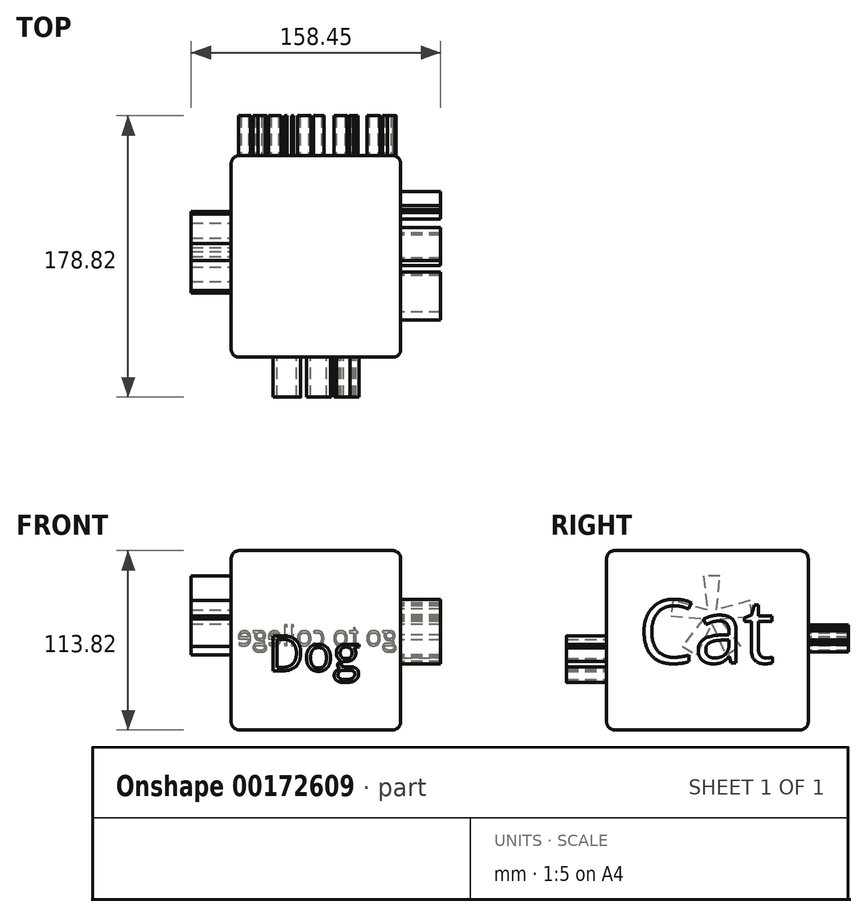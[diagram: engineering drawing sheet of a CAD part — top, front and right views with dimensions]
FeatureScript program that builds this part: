
annotation { "Feature Type Name" : "Feature", "Feature Type Description" : "" }
export const myFeature = defineFeature(function(context is Context, id is Id, definition is map)
    precondition{}
    {
        {
            var Q0;
            Q0=qCreatedBy(makeId("Front.planeOp"),FACE);
            var sketch = newSketch(context, id + "F0", { "sketchPlane" : qUnion([Q0])});
            skLineSegment(sketch, "E0.bottom", {"start": v(-56.12, 53.95) * mm, "end": v(51.53, 53.95) * mm});
            skLineSegment(sketch, "E0.top", {"start": v(-56.12, -59.87) * mm, "end": v(51.53, -59.87) * mm});
            skLineSegment(sketch, "E0.left", {"start": v(-56.12, 53.95) * mm, "end": v(-56.12, -59.87) * mm});
            skLineSegment(sketch, "E0.right", {"start": v(51.53, 53.95) * mm, "end": v(51.53, -59.87) * mm});
            skSolve(sketch);
        }
        {
            var Q0;
            Q0 = qSketchRegion(id + "F0", true);
            extrude(context, id + "F1", {"entities" : qUnion([Q0]), "depth" : 128.02 * mm});
        }
        {
            var Q0;
            Q0=makeQuery(id+"F1.opExtrude","SWEPT_EDGE",EDGE,{"disambiguationData":[OSD([sQuery(id+"F0.wireOp",EDGE,"E0.top"),sQuery(id+"F0.wireOp",EDGE,"E0.left")])]});
            var Q1;
            Q1=makeQuery(id+"F1.opExtrude","CAP_FACE",FACE,{"disambiguationData":[OSD([sQuery(id+"F0.wireOp",EDGE,"E0.bottom"),sQuery(id+"F0.wireOp",EDGE,"E0.top"),sQuery(id+"F0.wireOp",EDGE,"E0.left"),sQuery(id+"F0.wireOp",EDGE,"E0.right")])],"isStart":true});
            var Q2;
            Q2=makeQuery(id+"F1.opExtrude","SWEPT_EDGE",EDGE,{"disambiguationData":[OSD([sQuery(id+"F0.wireOp",EDGE,"E0.bottom"),sQuery(id+"F0.wireOp",EDGE,"E0.right")])]});
            var Q3;
            Q3=makeQuery(id+"F1.opExtrude","SWEPT_FACE",FACE,{"disambiguationData":[OSD([sQuery(id+"F0.wireOp",EDGE,"E0.bottom")])]});
            var Q4;
            Q4=makeQuery(id+"F1.opExtrude","SWEPT_EDGE",EDGE,{"disambiguationData":[OSD([sQuery(id+"F0.wireOp",EDGE,"E0.bottom"),sQuery(id+"F0.wireOp",EDGE,"E0.left")])]});
            var Q5;
            Q5=makeQuery(id+"F1.opExtrude","CAP_EDGE",EDGE,{"disambiguationData":[OSD([sQuery(id+"F0.wireOp",EDGE,"E0.bottom")])],"isStart":true});
            var Q6;
            Q6=makeQuery(id+"F1.opExtrude","SWEPT_FACE",FACE,{"disambiguationData":[OSD([sQuery(id+"F0.wireOp",EDGE,"E0.left")])]});
            var Q7;
            Q7=makeQuery(id+"F1.opExtrude","CAP_EDGE",EDGE,{"disambiguationData":[OSD([sQuery(id+"F0.wireOp",EDGE,"E0.bottom")])],"isStart":false});
            var Q8;
            Q8=makeQuery(id+"F1.opExtrude","CAP_EDGE",EDGE,{"disambiguationData":[OSD([sQuery(id+"F0.wireOp",EDGE,"E0.top")])],"isStart":true});
            var Q9;
            Q9=makeQuery(id+"F1.opExtrude","CAP_EDGE",EDGE,{"disambiguationData":[OSD([sQuery(id+"F0.wireOp",EDGE,"E0.right")])],"isStart":true});
            var Q10;
            Q10=makeQuery(id+"F1.opExtrude","CAP_EDGE",EDGE,{"disambiguationData":[OSD([sQuery(id+"F0.wireOp",EDGE,"E0.left")])],"isStart":true});
            var Q11;
            Q11=makeQuery(id+"F1.opExtrude","CAP_EDGE",EDGE,{"disambiguationData":[OSD([sQuery(id+"F0.wireOp",EDGE,"E0.left")])],"isStart":false});
            fillet(context, id + "F2", {"entities" : qUnion([Q0, Q1, Q2, Q3, Q4, Q5, Q6, Q7, Q8, Q9, Q10, Q11]), "radius" : 5.08 * mm, "tangentPropagation" : true, "allowEdgeOverflow" : false});
        }
        {
            var Q0;
            Q0=makeQuery(id+"F2.opFillet","BLEND_FACE",FACE,{"disambiguationData":[OSD([sQuery(id+"F0.wireOp",EDGE,"E0.right")])]});
            var Q1;
            Q1=makeQuery(id+"F1.opExtrude","SWEPT_FACE",FACE,{"disambiguationData":[OSD([sQuery(id+"F0.wireOp",EDGE,"E0.top")])]});
            var Q2;
            Q2=makeQuery(id+"F1.opExtrude","SWEPT_FACE",FACE,{"disambiguationData":[OSD([sQuery(id+"F0.wireOp",EDGE,"E0.right")])]});
            var Q3;
            Q3=makeQuery(id+"F1.opExtrude","SWEPT_EDGE",EDGE,{"disambiguationData":[OSD([sQuery(id+"F0.wireOp",EDGE,"E0.top"),sQuery(id+"F0.wireOp",EDGE,"E0.right")])]});
            var Q4;
            Q4=makeQuery(id+"F1.opExtrude","CAP_FACE",FACE,{"disambiguationData":[OSD([sQuery(id+"F0.wireOp",EDGE,"E0.bottom"),sQuery(id+"F0.wireOp",EDGE,"E0.top"),sQuery(id+"F0.wireOp",EDGE,"E0.left"),sQuery(id+"F0.wireOp",EDGE,"E0.right")])],"isStart":true});
            var Q5;
            {var subQ0=sQuery(id+"F0.wireOp",EDGE,"E0.right");Q5=makeQuery(id+"F2.opFillet","BLEND_EDGE",EDGE,{"blendedFrom":[makeQuery(id+"F1.opExtrude","CAP_EDGE",EDGE,{"disambiguationData":[OSD([subQ0])],"isStart":true}),makeQuery(id+"F1.opExtrude","CAP_FACE",FACE,{"disambiguationData":[OSD([sQuery(id+"F0.wireOp",EDGE,"E0.bottom"),sQuery(id+"F0.wireOp",EDGE,"E0.top"),sQuery(id+"F0.wireOp",EDGE,"E0.left"),subQ0])],"isStart":true})],"blendedInto":[makeQuery(id+"F1.opExtrude","CAP_FACE",FACE,{"disambiguationData":[OSD([sQuery(id+"F0.wireOp",EDGE,"E0.bottom"),sQuery(id+"F0.wireOp",EDGE,"E0.top"),sQuery(id+"F0.wireOp",EDGE,"E0.left"),subQ0])],"isStart":true})]});}
            var Q6;
            {var subQ0=sQuery(id+"F0.wireOp",EDGE,"E0.right");Q6=makeQuery(id+"F2.opFillet","BLEND_EDGE",EDGE,{"blendedFrom":[makeQuery(id+"F1.opExtrude","CAP_EDGE",EDGE,{"disambiguationData":[OSD([subQ0])],"isStart":true}),makeQuery(id+"F1.opExtrude","SWEPT_FACE",FACE,{"disambiguationData":[OSD([subQ0])]})],"blendedInto":[makeQuery(id+"F1.opExtrude","SWEPT_FACE",FACE,{"disambiguationData":[OSD([subQ0])]})]});}
            fillet(context, id + "F3", {"entities" : qUnion([Q0, Q1, Q2, Q3, Q4, Q5, Q6]), "radius" : 5.08 * mm, "tangentPropagation" : true, "allowEdgeOverflow" : false});
        }
        {
            var Q0;
            Q0=makeQuery(id+"F1.opExtrude","CAP_FACE",FACE,{"disambiguationData":[OSD([sQuery(id+"F0.wireOp",EDGE,"E0.bottom"),sQuery(id+"F0.wireOp",EDGE,"E0.top"),sQuery(id+"F0.wireOp",EDGE,"E0.left"),sQuery(id+"F0.wireOp",EDGE,"E0.right")])],"isStart":false});
            var sketch = newSketch(context, id + "F4", { "sketchPlane" : qUnion([Q0])});
            skText(sketch, "E1", { "text": "Dog", "fontName": "OpenSans-Regular.ttf"});
            const initialGuessF4  = {"E1": [-0.03277, -0.0224, 1, 0, 0.0224]};
            skSetInitialGuess(sketch, initialGuessF4);
            skSolve(sketch);
        }
        {
            var Q0;
            Q0 = qSketchRegion(id + "F4", true);
            extrude(context, id + "F5", {"entities" : qUnion([Q0]), "operationType" : NewBodyOperationType.ADD, "depth" : 25.4 * mm});
        }
        {
            var Q0;
            Q0=makeQuery(id+"F1.opExtrude","SWEPT_FACE",FACE,{"disambiguationData":[OSD([sQuery(id+"F0.wireOp",EDGE,"E0.right")])]});
            var sketch = newSketch(context, id + "F6", { "sketchPlane" : qUnion([Q0])});
            skText(sketch, "E2", { "text": "Cat", "fontName": "OpenSans-Regular.ttf"});
            const initialGuessF6  = {"E2": [-0.10773, -0.01741, 1, 0, 0.04031]};
            skSetInitialGuess(sketch, initialGuessF6);
            skSolve(sketch);
        }
        {
            var Q0;
            Q0 = qSketchRegion(id + "F6", true);
            extrude(context, id + "F7", {"entities" : qUnion([Q0]), "operationType" : NewBodyOperationType.ADD, "depth" : 25.4 * mm});
        }
        {
            var Q0;
            Q0=makeQuery(id+"F1.opExtrude","SWEPT_FACE",FACE,{"disambiguationData":[OSD([sQuery(id+"F0.wireOp",EDGE,"E0.left")])]});
            var sketch = newSketch(context, id + "F8", { "sketchPlane" : qUnion([Q0])});
            skText(sketch, "E3", { "text": "*", "fontName": "OpenSans-Regular.ttf"});
            const initialGuessF8  = {"E3": [0.03078, -0.04685, 1, 0, 0.08016]};
            skSetInitialGuess(sketch, initialGuessF8);
            skSolve(sketch);
        }
        {
            var Q0;
            Q0 = qSketchRegion(id + "F8", true);
            extrude(context, id + "F9", {"entities" : qUnion([Q0]), "operationType" : NewBodyOperationType.ADD, "depth" : 25.4 * mm});
        }
        {
            var Q0;
            Q0=makeQuery(id+"F1.opExtrude","CAP_FACE",FACE,{"disambiguationData":[OSD([sQuery(id+"F0.wireOp",EDGE,"E0.bottom"),sQuery(id+"F0.wireOp",EDGE,"E0.top"),sQuery(id+"F0.wireOp",EDGE,"E0.left"),sQuery(id+"F0.wireOp",EDGE,"E0.right")])],"isStart":true});
            var sketch = newSketch(context, id + "F10", { "sketchPlane" : qUnion([Q0])});
            skText(sketch, "E4", { "text": "go to college ", "fontName": "OpenSans-Regular.ttf"});
            const initialGuessF10  = {"E4": [-0.04893, -0.00634, 1, 0, 0.0124]};
            skSetInitialGuess(sketch, initialGuessF10);
            skSolve(sketch);
        }
        {
            var Q0;
            Q0 = qSketchRegion(id + "F10", true);
            extrude(context, id + "F11", {"entities" : qUnion([Q0]), "operationType" : NewBodyOperationType.ADD, "depth" : 25.4 * mm});
        }
    });
